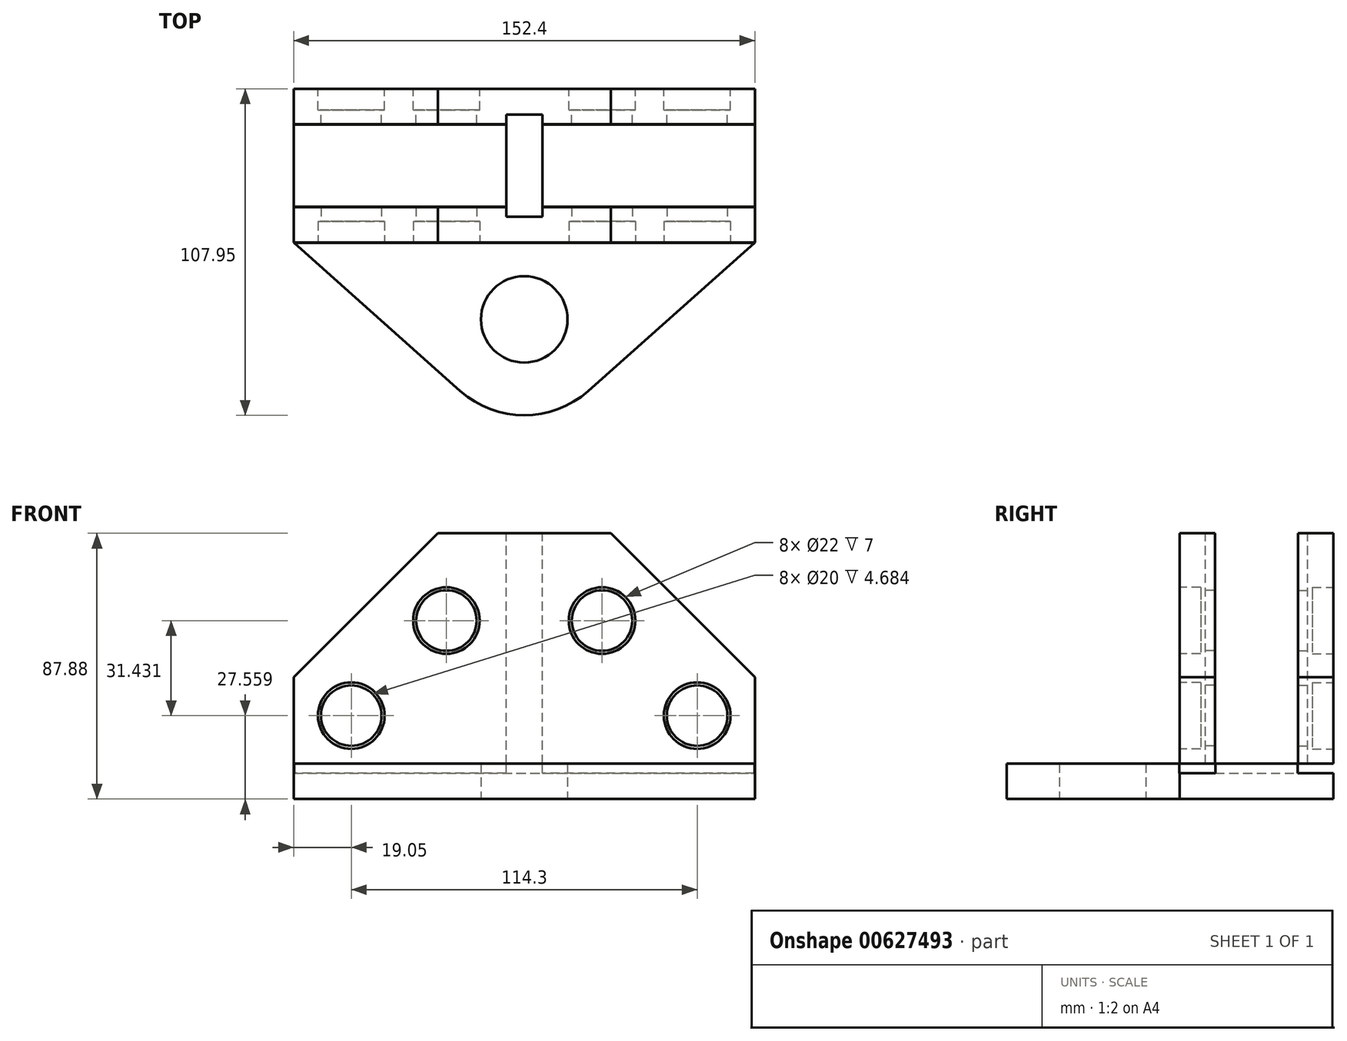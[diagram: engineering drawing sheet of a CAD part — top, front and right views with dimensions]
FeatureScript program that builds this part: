
annotation { "Feature Type Name" : "Feature", "Feature Type Description" : "" }
export const myFeature = defineFeature(function(context is Context, id is Id, definition is map)
    precondition{}
    {
        {
            var Q0;
            Q0=qCreatedBy(makeId("Top.planeOp"),FACE);
            var sketch = newSketch(context, id + "F0", { "sketchPlane" : qUnion([Q0])});
            skCircle(sketch, "E0", {"center": v(0, 0) * mm, "radius": 14.29 * mm});
            skArc(sketch, "E1", {"start": v(-21.13, -23.7) * mm, "mid": v(0, -31.75) * mm, "end": v(21.13, -23.7) * mm});
            skLineSegment(sketch, "E2", {"start": v(-21.13, -23.7) * mm, "end": v(-76.2, 25.4) * mm});
            skLineSegment(sketch, "E3", {"start": v(-76.2, 25.4) * mm, "end": v(-76.2, 76.2) * mm});
            skLineSegment(sketch, "E4", {"start": v(-76.2, 76.2) * mm, "end": v(76.2, 76.2) * mm});
            skLineSegment(sketch, "E5", {"start": v(21.13, -23.7) * mm, "end": v(76.2, 25.4) * mm});
            skLineSegment(sketch, "E6", {"start": v(76.2, 25.4) * mm, "end": v(76.2, 76.2) * mm});
            skSolve(sketch);
        }
        {
            var Q0;
            Q0 = qSketchRegion(id + "F0", true);
            extrude(context, id + "F1", {"entities" : qUnion([Q0]), "depth" : 11.68 * mm, "offsetDistance" : 25.4 * mm});
        }
        {
            var Q0;
            Q0=makeQuery(id+"F1.opExtrude","SWEPT_FACE",FACE,{"disambiguationData":[OSD([sQuery(id+"F0.wireOp",EDGE,"E4")])]});
            var sketch = newSketch(context, id + "F2", { "sketchPlane" : qUnion([Q0])});
            skLineSegment(sketch, "E7", {"start": v(-76.2, 8.5) * mm, "end": v(76.2, 8.5) * mm});
            skLineSegment(sketch, "E8", {"start": v(76.2, 8.5) * mm, "end": v(76.2, 40.26) * mm});
            skLineSegment(sketch, "E9", {"start": v(76.2, 40.26) * mm, "end": v(28.58, 87.88) * mm});
            skLineSegment(sketch, "E10", {"start": v(28.57, 87.88) * mm, "end": v(-28.57, 87.88) * mm});
            skLineSegment(sketch, "E11", {"start": v(-28.57, 87.88) * mm, "end": v(-76.2, 40.26) * mm});
            skLineSegment(sketch, "E12", {"start": v(-76.2, 40.26) * mm, "end": v(-76.2, 8.5) * mm});
            skSolve(sketch);
        }
        {
            var Q0;
            Q0 = qSketchRegion(id + "F2", true);
            extrude(context, id + "F3", {"entities" : qUnion([Q0]), "oppositeDirection" : true, "depth" : 11.68 * mm, "offsetDistance" : 25.4 * mm});
        }
        {
            var Q0;
            Q0=makeQuery(id+"F3.opExtrude","CAP_FACE",FACE,{"disambiguationData":[OSD([sQuery(id+"F2.wireOp",EDGE,"E7"),sQuery(id+"F2.wireOp",EDGE,"E8"),sQuery(id+"F2.wireOp",EDGE,"E9"),sQuery(id+"F2.wireOp",EDGE,"E10"),sQuery(id+"F2.wireOp",EDGE,"E11"),sQuery(id+"F2.wireOp",EDGE,"E12")])],"isStart":true});
            var sketch = newSketch(context, id + "F4", { "sketchPlane" : qUnion([Q0])});
            skCircle(sketch, "E13", {"center": v(-57.15, 27.56) * mm, "radius": 11 * mm});
            skCircle(sketch, "E14", {"center": v(-25.72, 58.99) * mm, "radius": 11 * mm});
            skCircle(sketch, "E15", {"center": v(25.72, 58.99) * mm, "radius": 11 * mm});
            skCircle(sketch, "E16", {"center": v(57.15, 27.56) * mm, "radius": 11 * mm});
            skLineSegment(sketch, "E17", {"start": v(-57.15, 27.56) * mm, "end": v(-25.72, 58.99) * mm, "construction": true});
            skSolve(sketch);
        }
        {
            var Q0;
            Q0 = qSketchRegion(id + "F4", true);
            extrude(context, id + "F5", {"entities" : qUnion([Q0]), "operationType" : NewBodyOperationType.REMOVE, "oppositeDirection" : true, "depth" : 7 * mm, "offsetDistance" : 25.4 * mm});
        }
        {
            var Q0;
            Q0=makeQuery(id+"F5.boolean.opBoolean","COPY",FACE,{"derivedFrom":makeQuery(id+"F5.opExtrude","CAP_FACE",FACE,{"disambiguationData":[OSD([sQuery(id+"F4.wireOp",EDGE,"E14")])],"isStart":false})});
            var sketch = newSketch(context, id + "F6", { "sketchPlane" : qUnion([Q0])});
            skCircle(sketch, "E18", {"center": v(-25.72, 58.99) * mm, "radius": 10 * mm});
            skCircle(sketch, "E19", {"center": v(-57.15, 27.56) * mm, "radius": 10 * mm});
            skCircle(sketch, "E20", {"center": v(25.72, 58.99) * mm, "radius": 10 * mm});
            skCircle(sketch, "E21", {"center": v(57.15, 27.56) * mm, "radius": 10 * mm});
            skSolve(sketch);
        }
        {
            var Q0;
            Q0 = qSketchRegion(id + "F6", true);
            extrude(context, id + "F7", {"entities" : qUnion([Q0]), "operationType" : NewBodyOperationType.REMOVE, "endBound" : BoundingType.UP_TO_NEXT, "oppositeDirection" : true, "depth" : 25.4 * mm, "offsetDistance" : 25.4 * mm});
        }
        {
            var Q0;
            Q0=makeQuery(id+"F1.opExtrude","CAP_EDGE",EDGE,{"disambiguationData":[OSD([sQuery(id+"F0.wireOp",EDGE,"E3")])],"isStart":false});
            cPoint(context, id + "F8", {"entities" : qUnion([Q0]), "parameter" : 0.5});
        }
        {
            var Q0;
            Q0=makeQuery(id+"F1.opExtrude","CAP_EDGE",EDGE,{"disambiguationData":[OSD([sQuery(id+"F0.wireOp",EDGE,"E3")])],"isStart":true});
            cPoint(context, id + "F9", {"entities" : qUnion([Q0]), "parameter" : 0.5});
        }
        {
            var Q0;
            Q0=makeQuery(id+"F1.opExtrude","CAP_EDGE",EDGE,{"disambiguationData":[OSD([sQuery(id+"F0.wireOp",EDGE,"E6")])],"isStart":false});
            cPoint(context, id + "F10", {"entities" : qUnion([Q0]), "parameter" : 0.5});
        }
        {
            var Q0;
            Q0 = qCreatedBy(id + "F8" ,VERTEX);
            var Q1;
            Q1 = qCreatedBy(id + "F9" ,VERTEX);
            var Q2;
            Q2 = qCreatedBy(id + "F10" ,VERTEX);
            cPlane(context, id + "F11", {"entities" : qUnion([Q0, Q1, Q2]), "cplaneType" : CPlaneType.THREE_POINT, "offset" : 25.4 * mm, "width" : 152.4 * mm, "height" : 152.4 * mm});
        }
        {
            var Q0;
            Q0=makeQuery(id+"F3.opExtrude","SWEPT_BODY",BODY,{"disambiguationData":[OSD([sQuery(id+"F2.wireOp",EDGE,"E7"),sQuery(id+"F2.wireOp",EDGE,"E8"),sQuery(id+"F2.wireOp",EDGE,"E9"),sQuery(id+"F2.wireOp",EDGE,"E10"),sQuery(id+"F2.wireOp",EDGE,"E11"),sQuery(id+"F2.wireOp",EDGE,"E12")])]});
            var Q1;
            Q1=qCreatedBy(id+"F11.planeOp",FACE);
            mirror(context, id + "F12", {"entities" : qUnion([Q0]), "mirrorPlane" : qUnion([Q1])});
        }
        {
            var Q0;
            Q0=makeQuery(id+"F12.opPattern","COPY",FACE,{"derivedFrom":makeQuery(id+"F3.opExtrude","SWEPT_FACE",FACE,{"disambiguationData":[OSD([sQuery(id+"F2.wireOp",EDGE,"E10")])]}),"instanceName":"1"});
            var sketch = newSketch(context, id + "F13", { "sketchPlane" : qUnion([Q0])});
            skLineSegment(sketch, "E22.bottom", {"start": v(-5.84, 67.7) * mm, "end": v(5.84, 67.7) * mm});
            skLineSegment(sketch, "E22.top", {"start": v(-5.84, 33.9) * mm, "end": v(5.84, 33.9) * mm});
            skLineSegment(sketch, "E22.left", {"start": v(-5.84, 67.7) * mm, "end": v(-5.84, 33.9) * mm});
            skLineSegment(sketch, "E22.right", {"start": v(5.84, 67.7) * mm, "end": v(5.84, 33.9) * mm});
            skSolve(sketch);
        }
        {
            var Q0;
            Q0 = qSketchRegion(id + "F13", true);
            var Q1;
            Q1=makeQuery(id+"F3.opExtrude","CAP_VERTEX",VERTEX,{"disambiguationData":[OSD([sQuery(id+"F0.wireOp",EDGE,"E4"),sQuery(id+"F0.wireOp",EDGE,"E6"),sQuery(id+"F2.wireOp",EDGE,"E7"),sQuery(id+"F2.wireOp",EDGE,"E12")])],"isStart":true});
            extrude(context, id + "F14", {"entities" : qUnion([Q0]), "endBound" : BoundingType.UP_TO_VERTEX, "oppositeDirection" : true, "depth" : 25.4 * mm, "endBoundEntityVertex" : qUnion([Q1]), "offsetDistance" : 25.4 * mm});
        }
        {
            var Q0;
            Q0=makeQuery(id+"F1.opExtrude","CAP_FACE",FACE,{"disambiguationData":[OSD([sQuery(id+"F0.wireOp",EDGE,"E0"),sQuery(id+"F0.wireOp",EDGE,"E1"),sQuery(id+"F0.wireOp",EDGE,"E2"),sQuery(id+"F0.wireOp",EDGE,"E3"),sQuery(id+"F0.wireOp",EDGE,"E4"),sQuery(id+"F0.wireOp",EDGE,"E5"),sQuery(id+"F0.wireOp",EDGE,"E6")])],"isStart":false});
            var sketch = newSketch(context, id + "F15", { "sketchPlane" : qUnion([Q0])});
            skLineSegment(sketch, "E23", {"start": v(-76.2, 76.2) * mm, "end": v(-76.2, 64.39) * mm});
            skLineSegment(sketch, "E24", {"start": v(-76.2, 64.39) * mm, "end": v(-5.97, 64.39) * mm});
            skLineSegment(sketch, "E25", {"start": v(-5.97, 64.39) * mm, "end": v(-5.97, 37.21) * mm});
            skLineSegment(sketch, "E26", {"start": v(-5.97, 37.21) * mm, "end": v(-76.2, 37.21) * mm});
            skLineSegment(sketch, "E27", {"start": v(-76.2, 37.21) * mm, "end": v(-76.2, 25.27) * mm});
            skLineSegment(sketch, "E28", {"start": v(-76.2, 25.27) * mm, "end": v(76.2, 25.27) * mm});
            skLineSegment(sketch, "E29", {"start": v(76.2, 25.27) * mm, "end": v(76.2, 37.21) * mm});
            skLineSegment(sketch, "E30", {"start": v(76.2, 37.21) * mm, "end": v(5.97, 37.21) * mm});
            skLineSegment(sketch, "E31", {"start": v(5.97, 37.21) * mm, "end": v(5.97, 64.39) * mm});
            skLineSegment(sketch, "E32", {"start": v(5.97, 64.39) * mm, "end": v(76.2, 64.39) * mm});
            skLineSegment(sketch, "E33", {"start": v(76.2, 64.39) * mm, "end": v(76.2, 76.2) * mm});
            skLineSegment(sketch, "E34", {"start": v(76.2, 76.2) * mm, "end": v(-76.2, 76.2) * mm});
            skSolve(sketch);
        }
        {
            var Q0;
            Q0 = qSketchRegion(id + "F15", true);
            var Q1;
            Q1=makeQuery(id+"F12.opPattern","COPY",VERTEX,{"derivedFrom":makeQuery(id+"F3.opExtrude","CAP_VERTEX",VERTEX,{"disambiguationData":[OSD([sQuery(id+"F0.wireOp",EDGE,"E3"),sQuery(id+"F0.wireOp",EDGE,"E4"),sQuery(id+"F2.wireOp",EDGE,"E7"),sQuery(id+"F2.wireOp",EDGE,"E8")])],"isStart":false}),"instanceName":"1"});
            extrude(context, id + "F16", {"entities" : qUnion([Q0]), "operationType" : NewBodyOperationType.REMOVE, "endBound" : BoundingType.UP_TO_VERTEX, "oppositeDirection" : true, "depth" : 25.4 * mm, "endBoundEntityVertex" : qUnion([Q1]), "offsetDistance" : 25.4 * mm});
        }
        {
            var Q0;
            Q0=makeQuery(id+"F3.opExtrude","SWEPT_FACE",FACE,{"disambiguationData":[OSD([sQuery(id+"F2.wireOp",EDGE,"E10")])]});
            var sketch = newSketch(context, id + "F17", { "sketchPlane" : qUnion([Q0])});
            skLineSegment(sketch, "E35.bottom", {"start": v(-5.97, 67.7) * mm, "end": v(5.97, 67.7) * mm});
            skLineSegment(sketch, "E35.top", {"start": v(-5.97, 33.9) * mm, "end": v(5.97, 33.9) * mm});
            skLineSegment(sketch, "E35.left", {"start": v(-5.97, 67.7) * mm, "end": v(-5.97, 33.9) * mm});
            skLineSegment(sketch, "E35.right", {"start": v(5.97, 67.7) * mm, "end": v(5.97, 33.9) * mm});
            skSolve(sketch);
        }
        {
            var Q0;
            Q0 = qSketchRegion(id + "F17", true);
            var Q1;
            Q1=makeQuery(id+"F16.boolean.opBoolean","COPY",VERTEX,{"derivedFrom":makeQuery(id+"F16.opExtrude","CAP_VERTEX",VERTEX,{"disambiguationData":[OSD([sQuery(id+"F15.wireOp",EDGE,"E23"),sQuery(id+"F15.wireOp",EDGE,"E34"),dummyQuery(id+"F16.vertexPlane.planeOp",FACE)])],"isStart":false})});
            extrude(context, id + "F18", {"entities" : qUnion([Q0]), "operationType" : NewBodyOperationType.REMOVE, "endBound" : BoundingType.UP_TO_VERTEX, "oppositeDirection" : true, "depth" : 25.4 * mm, "endBoundEntityVertex" : qUnion([Q1]), "offsetDistance" : 25.4 * mm});
        }
    });
